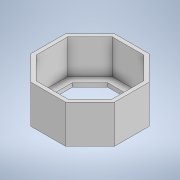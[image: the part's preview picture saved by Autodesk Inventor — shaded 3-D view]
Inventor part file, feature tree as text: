
AUTODESK INVENTOR PART (.ipt)
format: ipt  version: 2020 (Build 240168000, 168)  size: 331,264 bytes
history: native  units: mm
features: extrude x3, sketch x2
ambient origin geometry x8: Origin, YZ Plane, XZ Plane, XY Plane, X Axis, Y Axis, Z Axis, Center Point
bodies: Solid1 (feature_tree)
feature tree (5):
  sketch  "Sketch1"  dims[d0=8.25mm d3=8.25mm]
  extrude  "OutsideHeight"  Depth=8.25mm
  extrude  "BaseHeight"  Depth=1.0mm
  extrude  "BaseCut"  Depth=1.0mm
  sketch  "Sketch5"  dims[d5=8.25mm d7=8.25mm d8=8.25mm d9=8.25mm d12=8.25mm d17=8.25mm d29=1.0mm d31=1.0mm d32=1.0mm d33=1.0mm d34=10.0mm d35=0.0mm d36=1.0mm d37=0.0mm d57=2.0mm d66=2.0mm d72=2.0mm d94=135.0deg d95=135.0deg d101=135.0deg d102=135.0deg d110=135.0deg d115=135.0deg d116=135.0deg d125=135.0deg d126=135.0deg d127=135.0deg d128=135.0deg d129=135.0deg d130=135.0deg d131=2.0mm d132=1.0mm d133=0.0mm d135=1.0mm d138=1.0mm d139=135.0deg d140=135.0deg d141=135.0deg d142=135.0deg d143=1.0mm d144=1.0mm d145=135.0deg d146=135.0deg d147=135.0deg d148=135.0deg d149=135.0deg d150=135.0deg d151=135.0deg d152=135.0deg]
